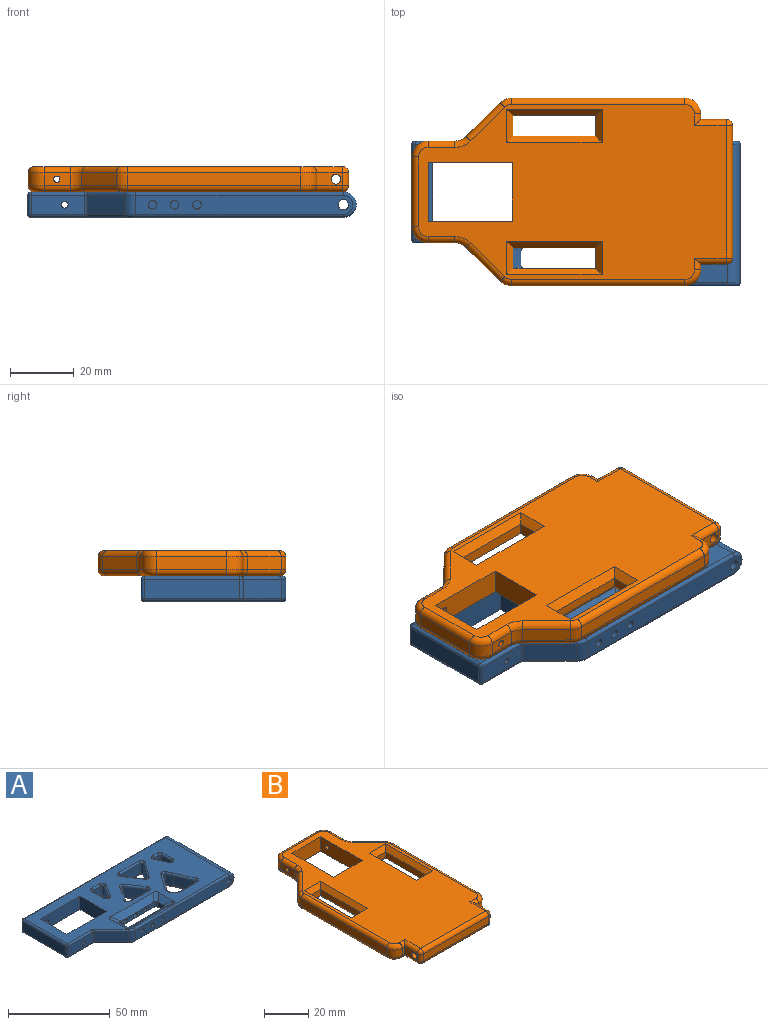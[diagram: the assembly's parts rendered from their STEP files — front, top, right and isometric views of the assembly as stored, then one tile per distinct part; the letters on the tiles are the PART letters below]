
ASSEMBLY  parts=2 mates=1
PART A: 177 faces, bbox 103.4x45.9x8.7 mm
  f0: cylinder r=1.05mm len=6.8mm, axis (0,1,0), area 44.9mm2, adj f19,f122
  f1: cylinder r=1.05mm len=6.8mm, axis (0,1,0), area 44.9mm2, adj f2,f79
  f2: plane 101.1x6mm, normal (0,1,0), area 590.7mm2, adj f1,f4,f5,f163,f164,f175
  f3: cylinder r=1mm len=65.22mm, axis (1,0,0), area 102.5mm2, adj f6,f8,f75,f165
  f4: cylinder r=1mm len=98.1mm, axis (1,0,0), area 154.1mm2, adj f2,f9,f163,f176
  f5: cylinder r=1mm len=98.1mm, axis (-1,0,0), area 154.1mm2, adj f2,f8,f163,f173
  f6: plane 68.22x6mm, normal (0,-1,0), area 379.7mm2, adj f3,f7,f76,f81,f83,f90,f164,f165
  f7: cylinder r=1mm len=65.22mm, axis (-1,0,0), area 102.5mm2, adj f6,f9,f77,f165
  f8: plane 98.1x43.5mm, normal (0,0,-1), area 2327mm2, adj f3,f5,f10,f11,f16,f17,f19,f25
  f9: plane 98.1x43.5mm, normal (0,0,1), area 2327mm2, adj f4,f7,f12,f13,f19,f20,f21,f22
  f10: cylinder r=1mm len=11.44mm, axis (0.59,0.81,0), area 21.1mm2, adj f8,f14,f93,f148
  f11: cylinder r=1mm len=11.98mm, axis (-1,0,0), area 18.8mm2, adj f8,f15,f97,f135
  f12: cylinder r=1mm len=11.98mm, axis (1,0,0), area 18.8mm2, adj f9,f15,f31,f136
  f13: cylinder r=1mm len=11.44mm, axis (-0.59,-0.81,0), area 21.1mm2, adj f9,f14,f95,f150
  f14: plane 10.85x7.9mm, normal (0.81,-0.59,0), area 80.5mm2, adj f10,f13,f92,f143
  f15: plane 11.98x6mm, normal (0,1,0), area 71.9mm2, adj f11,f12,f130,f138
  f16: cylinder r=3mm len=5.62mm, axis (0.63,-0.63,0.44), area 14mm2, adj f8,f17,f24,f68,f84,f88
  f17: plane 10.2x3.57mm, normal (0.57,0,-0.82), area 28.9mm2, adj f8,f16,f25,f88
  f18: cylinder r=1mm len=6mm, axis (0,0,-1), area 4.7mm2, adj f69,f70,f102,f122
  f19: plane 27.5x8mm, normal (0,1,0), area 216.5mm2, adj f0,f8,f9,f80,f168
  f20: plane 29.7x3.57mm, normal (0,0.57,0.82), area 113.9mm2, adj f9,f82,f101,f107
  f21: cylinder r=1mm len=7.99mm, axis (0,-1,0), area 12.5mm2, adj f9,f48,f49,f126
  f22: cylinder r=3mm len=5.62mm, axis (-0.63,-0.63,-0.44), area 14mm2, adj f9,f23,f27,f84,f87,f91
  f23: cylinder r=1mm len=3.12mm, axis (0,0,-1), area 4.9mm2, adj f22,f27,f84,f131
  f24: cylinder r=1mm len=3.12mm, axis (0,0,-1), area 4.9mm2, adj f16,f84,f88,f132
  f25: cylinder r=3mm len=5.62mm, axis (0.63,0.63,0.44), area 14mm2, adj f8,f17,f30,f82,f85,f88
  f26: torus R=2mm, axis (0,0,-1), area 4.6mm2, adj f9,f46,f47,f105
  f27: plane 4.52x3.14mm, normal (-1,0,0), area 13.6mm2, adj f22,f23,f86,f87,f99,f100,f101,f131
  f28: torus R=2mm, axis (0,0,-1), area 4.2mm2, adj f9,f64,f67,f106
  f29: cylinder r=1mm len=1mm, axis (0,-1,0), area 1.5mm2, adj f9,f32,f95,f124
  f30: cylinder r=1mm len=3.12mm, axis (0,0,-1), area 4.9mm2, adj f25,f82,f88,f107
  f31: torus R=2mm, axis (0,0,-1), area 1.7mm2, adj f9,f12,f33,f130
  f32: torus R=2mm, axis (0,0,-1), area 1.7mm2, adj f9,f29,f33,f129
  f33: cylinder r=1mm len=3.12mm, axis (0.71,-0.71,0), area 5.4mm2, adj f9,f31,f32,f121
  f34: torus R=2mm, axis (0,0,-1), area 4.7mm2, adj f8,f35,f36,f118
  f35: cylinder r=1mm len=13.73mm, axis (1,0,0), area 21.6mm2, adj f8,f34,f37,f125
  f36: cylinder r=1mm len=10.38mm, axis (-0.59,-0.81,0), area 19mm2, adj f8,f34,f38,f112
  f37: torus R=2mm, axis (0,0,-1), area 4.6mm2, adj f8,f35,f39,f119
  f38: torus R=2mm, axis (0,0,-1), area 4.1mm2, adj f8,f36,f39,f116
  f39: cylinder r=1mm len=10.35mm, axis (-0.56,0.83,0), area 18.5mm2, adj f8,f37,f38,f113
  f40: torus R=2mm, axis (0,0,-1), area 4.6mm2, adj f8,f41,f42,f105
  f41: cylinder r=1mm len=5.32mm, axis (1,0,0), area 8.4mm2, adj f8,f40,f43,f89
  f42: cylinder r=1mm len=8.54mm, axis (-0.55,-0.83,0), area 15.1mm2, adj f8,f40,f44,f117
  f43: torus R=2mm, axis (0,0,-1), area 3.4mm2, adj f8,f41,f45,f120
  f44: torus R=2mm, axis (0,0,-1), area 5.5mm2, adj f8,f42,f45,f110
  f45: cylinder r=1mm len=7.99mm, axis (0,1,0), area 12.5mm2, adj f8,f43,f44,f126
  f46: cylinder r=1mm len=8.54mm, axis (0.55,0.83,0), area 15.1mm2, adj f9,f26,f48,f117
  f47: cylinder r=1mm len=5.32mm, axis (-1,0,0), area 8.4mm2, adj f9,f26,f49,f89
  f48: torus R=2mm, axis (0,0,-1), area 5.5mm2, adj f9,f21,f46,f110
  f49: torus R=2mm, axis (0,0,-1), area 3.4mm2, adj f9,f21,f47,f120
  f50: torus R=2mm, axis (0,0,-1), area 4.7mm2, adj f9,f51,f52,f118
  f51: cylinder r=1mm len=10.38mm, axis (0.59,0.81,0), area 19mm2, adj f9,f50,f53,f112
  f52: cylinder r=1mm len=13.73mm, axis (-1,0,0), area 21.6mm2, adj f9,f50,f54,f125
  f53: torus R=2mm, axis (0,0,-1), area 4.1mm2, adj f9,f51,f55,f116
  f54: torus R=2mm, axis (0,0,-1), area 4.6mm2, adj f9,f52,f55,f119
  f55: cylinder r=1mm len=10.35mm, axis (0.56,-0.83,0), area 18.5mm2, adj f9,f53,f54,f113
  f56: cylinder r=1mm len=6mm, axis (0,0,1), area 13mm2, adj f60,f66,f114,f115
  f57: torus R=2mm, axis (0,0,-1), area 4.6mm2, adj f8,f58,f59,f109
  f58: cylinder r=1mm len=12.77mm, axis (-1,0,0), area 20.1mm2, adj f8,f57,f60,f114
  f59: cylinder r=1mm len=10.08mm, axis (0.55,0.83,0), area 18mm2, adj f8,f57,f61,f123
  f60: torus R=2mm, axis (0,0,-1), area 4.6mm2, adj f8,f56,f58,f62
  f61: torus R=2mm, axis (0,0,-1), area 4.2mm2, adj f8,f59,f62,f106
  f62: cylinder r=1mm len=10.08mm, axis (0.56,-0.83,0), area 18mm2, adj f8,f60,f61,f115
  f63: torus R=2mm, axis (0,0,-1), area 4.6mm2, adj f9,f64,f65,f109
  f64: cylinder r=1mm len=10.08mm, axis (-0.55,-0.83,0), area 18mm2, adj f9,f28,f63,f123
  f65: cylinder r=1mm len=12.77mm, axis (1,0,0), area 20.1mm2, adj f9,f63,f66,f114
  f66: torus R=2mm, axis (0,0,-1), area 4.6mm2, adj f9,f56,f65,f67
  f67: cylinder r=1mm len=10.08mm, axis (-0.56,0.83,0), area 18mm2, adj f9,f28,f66,f115
  f68: plane 29.7x3.57mm, normal (0,-0.57,-0.82), area 113.9mm2, adj f8,f16,f84,f131
  f69: torus R=2mm, axis (0,0,-1), area 1.7mm2, adj f8,f18,f71,f72
  f70: torus R=2mm, axis (0,0,-1), area 1.7mm2, adj f9,f18,f73,f74
  f71: cylinder r=1mm len=16.89mm, axis (1,0,0), area 26.5mm2, adj f8,f69,f122,f169
  f72: cylinder r=1mm len=12.45mm, axis (0.71,-0.71,0), area 26.1mm2, adj f8,f69,f75,f102
  f73: cylinder r=1mm len=12.45mm, axis (-0.71,0.71,0), area 26.1mm2, adj f9,f70,f77,f102
  f74: cylinder r=1mm len=16.89mm, axis (-1,0,0), area 26.5mm2, adj f9,f70,f122,f172
  f75: torus R=4mm, axis (0,0,-1), area 5.7mm2, adj f3,f8,f72,f76
  f76: cylinder r=5mm len=6mm, axis (0,0,1), area 23.6mm2, adj f6,f75,f77,f102
  f77: torus R=4mm, axis (0,0,-1), area 5.7mm2, adj f7,f9,f73,f76
  f78: plane 2.7x2.7mm, normal (0,-1,0), area 5.7mm2, adj f127
  f79: plane 27.5x8mm, normal (0,-1,0), area 216.5mm2, adj f1,f8,f9,f80,f168
  f80: plane 18.4x8mm, normal (-1,0,0), area 147.2mm2, adj f8,f9,f19,f79
  f81: cylinder r=1.35mm len=5.5mm, axis (0,1,0), area 46.7mm2, adj f6,f82
  f82: plane 24.02x3.14mm, normal (0,1,0), area 54.9mm2, adj f20,f25,f30,f81,f83,f85,f90,f99
  f83: cylinder r=1.35mm len=5.5mm, axis (0,1,0), area 46.7mm2, adj f6,f82
  f84: plane 24.02x3.14mm, normal (0,-1,0), area 54.9mm2, adj f16,f22,f23,f24,f68,f91,f103,f108
  f85: plane 29.7x3.57mm, normal (0,0.57,-0.82), area 113.9mm2, adj f8,f25,f82,f99
  f86: plane 10.2x3.57mm, normal (-0.57,0,-0.82), area 28.9mm2, adj f8,f27,f99,f131
  f87: plane 10.2x3.57mm, normal (-0.57,0,0.82), area 28.9mm2, adj f9,f22,f27,f101
  f88: plane 4.52x3.14mm, normal (1,0,0), area 13.6mm2, adj f16,f17,f24,f25,f30,f107,f128,f132
  f89: plane 6x5.32mm, normal (0,-1,0), area 31.9mm2, adj f41,f47,f105,f120
  f90: cylinder r=1.35mm len=5.5mm, axis (0,1,0), area 46.7mm2, adj f6,f82
  f91: plane 29.7x3.57mm, normal (0,-0.57,0.82), area 113.9mm2, adj f9,f22,f84,f132
  f92: cylinder r=1mm len=6mm, axis (0,0,-1), area 3.8mm2, adj f14,f93,f95,f124
  f93: torus R=2mm, axis (0,0,-1), area 1.3mm2, adj f8,f10,f92,f94
  f94: cylinder r=1mm len=1mm, axis (0,1,0), area 1.5mm2, adj f8,f93,f98,f124
  f95: torus R=2mm, axis (0,0,-1), area 1.3mm2, adj f9,f13,f29,f92
  f96: cylinder r=1mm len=3.12mm, axis (-0.71,0.71,0), area 5.4mm2, adj f8,f97,f98,f121
  f97: torus R=2mm, axis (0,0,-1), area 1.7mm2, adj f8,f11,f96,f130
  f98: torus R=2mm, axis (0,0,-1), area 1.7mm2, adj f8,f94,f96,f129
  f99: cylinder r=3mm len=5.62mm, axis (-0.63,0.63,0.44), area 14mm2, adj f8,f27,f82,f85,f86,f100
  f100: cylinder r=1mm len=3.12mm, axis (0,0,-1), area 4.9mm2, adj f27,f82,f99,f101
  f101: cylinder r=3mm len=5.62mm, axis (-0.63,0.63,-0.44), area 14mm2, adj f9,f20,f27,f82,f87,f100
  f102: plane 11.74x11.74mm, normal (-0.71,-0.71,0), area 99.6mm2, adj f18,f72,f73,f76
  f103: cylinder r=1.35mm len=4.5mm, axis (0,1,0), area 38.2mm2, adj f84,f104
  f104: plane 2.7x2.7mm, normal (0,-1,0), area 5.7mm2, adj f103
  f105: cylinder r=1mm len=6mm, axis (0,0,-1), area 13mm2, adj f26,f40,f89,f117
  f106: cylinder r=1mm len=6mm, axis (0,0,-1), area 11.8mm2, adj f28,f61,f115,f123
  f107: cylinder r=3mm len=5.62mm, axis (0.63,0.63,-0.44), area 14mm2, adj f9,f20,f30,f82,f88,f128
  f108: cylinder r=1.35mm len=4.5mm, axis (0,1,0), area 38.2mm2, adj f84,f111
  f109: cylinder r=1mm len=6mm, axis (0,0,-1), area 13mm2, adj f57,f63,f114,f123
  f110: cylinder r=1mm len=6mm, axis (0,0,1), area 15.3mm2, adj f44,f48,f117,f126
  f111: plane 2.7x2.7mm, normal (0,-1,0), area 5.7mm2, adj f108
  f112: plane 9.79x7.13mm, normal (-0.81,0.59,0), area 72.7mm2, adj f36,f51,f116,f118
  f113: plane 9.79x6.6mm, normal (0.83,0.56,0), area 70.9mm2, adj f39,f55,f116,f119
  f114: plane 12.77x6mm, normal (0,1,0), area 76.6mm2, adj f56,f58,f65,f109
  f115: plane 9.52x6.42mm, normal (-0.83,-0.56,0), area 68.9mm2, adj f56,f62,f67,f106
  f116: cylinder r=1mm len=6mm, axis (0,0,1), area 11.5mm2, adj f38,f53,f112,f113
  f117: plane 7.99x6mm, normal (-0.83,0.55,0), area 57.6mm2, adj f42,f46,f105,f110
  f118: cylinder r=1mm len=6mm, axis (0,0,-1), area 13.2mm2, adj f34,f50,f112,f125
  f119: cylinder r=1mm len=6mm, axis (0,0,1), area 13mm2, adj f37,f54,f113,f125
  f120: cylinder r=1mm len=6mm, axis (0,0,-1), area 9.4mm2, adj f43,f49,f89,f126
  f121: plane 6x2.41mm, normal (0.71,0.71,0), area 20.5mm2, adj f33,f96,f129,f130
  f122: plane 16.89x6mm, normal (0,-1,0), area 97.9mm2, adj f0,f18,f71,f74,f170
  f123: plane 9.52x6.35mm, normal (0.83,-0.55,0), area 68.7mm2, adj f59,f64,f106,f109
  f124: plane 6x0.97mm, normal (1,0,0), area 5.8mm2, adj f29,f92,f94,f129
  f125: plane 13.73x6mm, normal (0,-1,0), area 82.4mm2, adj f35,f52,f118,f119
  f126: plane 7.99x6mm, normal (1,0,0), area 47.9mm2, adj f21,f45,f110,f120
  f127: cylinder r=1.35mm len=4.5mm, axis (0,1,0), area 38.2mm2, adj f78,f84
  f128: plane 10.2x3.57mm, normal (0.57,0,0.82), area 28.9mm2, adj f9,f88,f107,f132
  f129: cylinder r=1mm len=6mm, axis (0,0,-1), area 4.7mm2, adj f32,f98,f121,f124
  f130: cylinder r=1mm len=6mm, axis (0,0,-1), area 4.7mm2, adj f15,f31,f97,f121
  f131: cylinder r=3mm len=5.62mm, axis (-0.63,-0.63,0.44), area 14mm2, adj f8,f23,f27,f68,f84,f86
  f132: cylinder r=3mm len=5.62mm, axis (0.63,-0.63,-0.44), area 14mm2, adj f9,f24,f84,f88,f91,f128
  f133: plane 10.64x6mm, normal (-0.91,-0.42,0), area 70.2mm2, adj f134,f137,f138,f139
  f134: cylinder r=1mm len=13.05mm, axis (0.42,-0.91,0), area 20.1mm2, adj f8,f133,f135,f147
  f135: torus R=2mm, axis (0,0,-1), area 4.3mm2, adj f8,f11,f134,f138
  f136: torus R=2mm, axis (0,0,-1), area 4.3mm2, adj f9,f12,f137,f138
  f137: cylinder r=1mm len=13.05mm, axis (-0.42,0.91,0), area 20.1mm2, adj f9,f133,f136,f149
  f138: cylinder r=1mm len=6mm, axis (0,0,1), area 12mm2, adj f15,f133,f135,f136
  f139: plane 6x3.59mm, normal (-0.91,-0.42,0), area 23.7mm2, adj f133,f143,f147,f149
  f140: plane 6x3.11mm, normal (0,-1,0), area 18.6mm2, adj f144,f146,f154,f160
  f141: plane 6.81x6mm, normal (-1,0,0), area 40.9mm2, adj f145,f146,f151,f161
  f142: plane 6.81x6mm, normal (0.91,0.42,0), area 44.9mm2, adj f144,f145,f155,f157
  f143: cylinder r=1mm len=6mm, axis (0,0,1), area 12.5mm2, adj f14,f139,f148,f150
  f144: cylinder r=1mm len=6mm, axis (0,0,-1), area 12mm2, adj f140,f142,f156,f158
  f145: cylinder r=1mm len=6mm, axis (0,0,-1), area 16.3mm2, adj f141,f142,f153,f159
  f146: cylinder r=1mm len=6mm, axis (0,0,-1), area 9.4mm2, adj f140,f141,f152,f162
  f147: cylinder r=1mm len=4.01mm, axis (0.42,-0.91,0), area 4.5mm2, adj f8,f134,f139,f148
  f148: torus R=2mm, axis (0,0,-1), area 4.5mm2, adj f8,f10,f143,f147
  f149: cylinder r=1mm len=4.01mm, axis (-0.42,0.91,0), area 4.5mm2, adj f9,f137,f139,f150
  f150: torus R=2mm, axis (0,0,-1), area 4.5mm2, adj f9,f13,f143,f149
  f151: cylinder r=1mm len=6.81mm, axis (0,-1,0), area 10.7mm2, adj f8,f141,f152,f153
  f152: torus R=2mm, axis (0,0,-1), area 3.4mm2, adj f8,f146,f151,f154
  f153: torus R=2mm, axis (0,0,-1), area 5.8mm2, adj f8,f145,f151,f155
  f154: cylinder r=1mm len=3.11mm, axis (1,0,0), area 4.9mm2, adj f8,f140,f152,f156
  f155: cylinder r=1mm len=7.22mm, axis (-0.42,0.91,0), area 11.8mm2, adj f8,f142,f153,f156
  f156: torus R=2mm, axis (0,0,-1), area 4.3mm2, adj f8,f144,f154,f155
  f157: cylinder r=1mm len=7.22mm, axis (0.42,-0.91,0), area 11.8mm2, adj f9,f142,f158,f159
  f158: torus R=2mm, axis (0,0,-1), area 4.3mm2, adj f9,f144,f157,f160
  f159: torus R=2mm, axis (0,0,-1), area 5.8mm2, adj f9,f145,f157,f161
  f160: cylinder r=1mm len=3.11mm, axis (-1,0,0), area 4.9mm2, adj f9,f140,f158,f162
  f161: cylinder r=1mm len=6.81mm, axis (0,1,0), area 10.7mm2, adj f9,f141,f159,f162
  f162: torus R=2mm, axis (0,0,-1), area 3.4mm2, adj f9,f146,f160,f161
  f163: torus R=3mm, axis (0,-1,0), area 17.9mm2, adj f2,f4,f5,f166
  f164: cylinder r=1.65mm len=45.5mm, axis (0,1,0), area 471.7mm2, adj f2,f6
  f165: torus R=3mm, axis (0,1,0), area 17.9mm2, adj f3,f6,f7,f166
  f166: cylinder r=4mm len=43.5mm, axis (0,1,0), area 546.6mm2, adj f8,f9,f163,f165
  f167: plane 30x6mm, normal (-1,0,0), area 180mm2, adj f170,f171,f174,f175
  f168: plane 18.4x8mm, normal (1,0,0), area 147.2mm2, adj f8,f9,f19,f79
  f169: sphere r=1mm, area 1.6mm2, adj f71,f170,f171
  f170: cylinder r=1mm len=6mm, axis (0,0,1), area 9.4mm2, adj f122,f167,f169,f172
  f171: cylinder r=1mm len=30mm, axis (0,1,0), area 47.1mm2, adj f8,f167,f169,f173
  f172: sphere r=1mm, area 1.6mm2, adj f74,f170,f174
  f173: sphere r=1mm, area 2.1mm2, adj f5,f171,f175
  f174: cylinder r=1mm len=30mm, axis (0,1,0), area 47.1mm2, adj f9,f167,f172,f176
  f175: cylinder r=1mm len=6mm, axis (0,0,1), area 9.4mm2, adj f2,f167,f173,f176
  f176: sphere r=1mm, area 2.1mm2, adj f4,f174,f175
PART B: 99 faces, bbox 59.8x101x8 mm
  f0: plane 18.4x8mm, normal (0,1,0), area 147.2mm2, adj f1,f14,f15,f16
  f1: plane 26.5x8mm, normal (1,0,0), area 208.9mm2, adj f0,f2,f14,f15,f28
  f2: plane 18.4x8mm, normal (0,-1,0), area 147.2mm2, adj f1,f14,f15,f16
  f3: plane 21.97x4mm, normal (0,1,0), area 87.9mm2, adj f29,f33,f38,f55
  f4: plane 8.37x4mm, normal (-1,0,0), area 30.4mm2, adj f28,f33,f34,f39,f47
  f5: plane 10.83x10.63mm, normal (-0.71,0.7,0), area 60.7mm2, adj f34,f35,f43,f50
  f6: plane 54.42x4mm, normal (-1,0,0), area 217.7mm2, adj f35,f36,f49,f58
  f7: plane 4x1.73mm, normal (0,-1,0), area 6.9mm2, adj f8,f36,f57,f66
  f8: plane 8x4mm, normal (-1,0,0), area 24.9mm2, adj f7,f26,f61,f70,f71
  f9: plane 26x3mm, normal (-1,0,0), area 78mm2, adj f10,f12,f88,f96
  f10: plane 6.5x3mm, normal (0,1,0), area 19.5mm2, adj f9,f11,f90,f98
  f11: plane 26x3mm, normal (1,0,0), area 78mm2, adj f10,f12,f89,f97
  f12: plane 7.3x3.5mm, normal (0,-1,0), area 22.9mm2, adj f9,f11,f87,f88,f89,f95
  f13: plane 41.5x4mm, normal (0,-1,0), area 166mm2, adj f69,f70,f76,f77
  f14: plane 96.62x54.96mm, normal (0,0,1), area 3482.5mm2, adj f0,f1,f2,f16,f46,f47,f50,f51
  f15: plane 96.62x54.96mm, normal (0,0,-1), area 3456.8mm2, adj f0,f1,f2,f16,f37,f38,f39,f40
  f16: plane 26.5x8mm, normal (-1,0,0), area 208.9mm2, adj f0,f2,f14,f15,f27
  f17: plane 8.37x4mm, normal (1,0,0), area 30.4mm2, adj f27,f29,f30,f42,f63
  f18: plane 10.83x10.63mm, normal (0.71,0.7,0), area 60.7mm2, adj f30,f31,f48,f72
  f19: plane 54.42x4mm, normal (1,0,0), area 217.7mm2, adj f31,f32,f56,f78
  f20: plane 4x1.73mm, normal (0,-1,0), area 6.9mm2, adj f21,f32,f64,f82
  f21: plane 8x4mm, normal (1,0,0), area 24.9mm2, adj f20,f26,f68,f76,f81
  f22: plane 26x3mm, normal (1,0,0), area 78mm2, adj f23,f25,f84,f91
  f23: plane 6.9x3.5mm, normal (0,1,0), area 22.9mm2, adj f22,f24,f84,f86,f92
  f24: plane 26.4x3.5mm, normal (-1,0,0), area 91.1mm2, adj f23,f25,f83,f85,f94
  f25: plane 6.5x3mm, normal (0,-1,0), area 19.5mm2, adj f22,f24,f83,f93
  f26: cylinder r=1.5mm len=45.5mm, axis (1,0,0), area 428.8mm2, adj f8,f21
  f27: cylinder r=1mm len=6.79mm, axis (1,0,0), area 42.6mm2, adj f16,f17
  f28: cylinder r=1mm len=6.79mm, axis (1,0,0), area 42.6mm2, adj f1,f4
  f29: cylinder r=5mm len=5mm, axis (0,0,-1), area 31.4mm2, adj f3,f17,f40,f59
  f30: cylinder r=5mm len=4mm, axis (0,0,1), area 15.5mm2, adj f17,f18,f44,f67
  f31: cylinder r=5mm len=4mm, axis (0,0,-1), area 15.5mm2, adj f18,f19,f52,f75
  f32: cylinder r=5mm len=5mm, axis (0,0,-1), area 31.4mm2, adj f19,f20,f60,f80
  f33: cylinder r=5mm len=5mm, axis (0,0,-1), area 31.4mm2, adj f3,f4,f37,f51
  f34: cylinder r=5mm len=4mm, axis (0,0,1), area 15.5mm2, adj f4,f5,f41,f46
  f35: cylinder r=5mm len=4mm, axis (0,0,-1), area 15.5mm2, adj f5,f6,f45,f54
  f36: cylinder r=5mm len=5mm, axis (0,0,-1), area 31.4mm2, adj f6,f7,f53,f62
  f37: torus R=3mm, axis (0,0,1), area 21.1mm2, adj f15,f33,f38,f39
  f38: cylinder r=2mm len=21.97mm, axis (-1,0,0), area 69mm2, adj f3,f15,f37,f40
  f39: cylinder r=2mm len=8.37mm, axis (0,-1,0), area 26.3mm2, adj f4,f15,f37,f41
  f40: torus R=3mm, axis (0,0,1), area 21.1mm2, adj f15,f29,f38,f42
  f41: torus R=7mm, axis (0,0,1), area 14mm2, adj f15,f34,f39,f43
  f42: cylinder r=2mm len=8.37mm, axis (0,-1,0), area 26.3mm2, adj f15,f17,f40,f44
  f43: cylinder r=2mm len=12.23mm, axis (-0.7,-0.71,0), area 47.7mm2, adj f5,f15,f41,f45
  f44: torus R=7mm, axis (0,0,1), area 14mm2, adj f15,f30,f42,f48
  f45: torus R=3mm, axis (0,0,1), area 10.4mm2, adj f15,f35,f43,f49
  f46: torus R=7mm, axis (0,0,1), area 14mm2, adj f14,f34,f47,f50
  f47: cylinder r=2mm len=8.37mm, axis (0,1,0), area 26.3mm2, adj f4,f14,f46,f51
  f48: cylinder r=2mm len=12.23mm, axis (0.7,-0.71,0), area 47.7mm2, adj f15,f18,f44,f52
  f49: cylinder r=2mm len=54.42mm, axis (0,-1,0), area 171mm2, adj f6,f15,f45,f53
  f50: cylinder r=2mm len=12.23mm, axis (0.7,0.71,0), area 47.7mm2, adj f5,f14,f46,f54
  f51: torus R=3mm, axis (0,0,1), area 21.1mm2, adj f14,f33,f47,f55
  f52: torus R=3mm, axis (0,0,1), area 10.4mm2, adj f15,f31,f48,f56
  f53: torus R=3mm, axis (0,0,1), area 21.1mm2, adj f15,f36,f49,f57
  f54: torus R=3mm, axis (0,0,1), area 10.4mm2, adj f14,f35,f50,f58
  f55: cylinder r=2mm len=21.97mm, axis (1,0,0), area 69mm2, adj f3,f14,f51,f59
  f56: cylinder r=2mm len=54.42mm, axis (0,-1,0), area 171mm2, adj f15,f19,f52,f60
  f57: cylinder r=2mm len=3.73mm, axis (1,0,0), area 7.7mm2, adj f7,f15,f53,f61
  f58: cylinder r=2mm len=54.42mm, axis (0,1,0), area 171mm2, adj f6,f14,f54,f62
  f59: torus R=3mm, axis (0,0,1), area 21.1mm2, adj f14,f29,f55,f63
  f60: torus R=3mm, axis (0,0,1), area 21.1mm2, adj f15,f32,f56,f64
  f61: cylinder r=2mm len=10mm, axis (0,-1,0), area 27.4mm2, adj f8,f15,f57,f65
  f62: torus R=3mm, axis (0,0,1), area 21.1mm2, adj f14,f36,f58,f66
  f63: cylinder r=2mm len=8.37mm, axis (0,1,0), area 26.3mm2, adj f14,f17,f59,f67
  f64: cylinder r=2mm len=3.73mm, axis (-1,0,0), area 7.7mm2, adj f15,f20,f60,f68
  f65: sphere r=2mm, area 6.3mm2, adj f61,f69,f70
  f66: cylinder r=2mm len=3.73mm, axis (-1,0,0), area 7.7mm2, adj f7,f14,f62,f71
  f67: torus R=7mm, axis (0,0,1), area 14mm2, adj f14,f30,f63,f72
  f68: cylinder r=2mm len=10mm, axis (0,-1,0), area 27.4mm2, adj f15,f21,f64,f73
  f69: cylinder r=2mm len=41.5mm, axis (1,0,0), area 130.4mm2, adj f13,f15,f65,f73
  f70: cylinder r=2mm len=4mm, axis (0,0,-1), area 12.6mm2, adj f8,f13,f65,f74
  f71: cylinder r=2mm len=10mm, axis (0,1,0), area 27.4mm2, adj f8,f14,f66,f74
  f72: cylinder r=2mm len=12.23mm, axis (-0.7,0.71,0), area 47.7mm2, adj f14,f18,f67,f75
  f73: sphere r=2mm, area 6.3mm2, adj f68,f69,f76
  f74: sphere r=2mm, area 6.3mm2, adj f70,f71,f77
  f75: torus R=3mm, axis (0,0,1), area 10.4mm2, adj f14,f31,f72,f78
  f76: cylinder r=2mm len=4mm, axis (0,0,-1), area 12.6mm2, adj f13,f21,f73,f79
  f77: cylinder r=2mm len=41.5mm, axis (-1,0,0), area 130.4mm2, adj f13,f14,f74,f79
  f78: cylinder r=2mm len=54.42mm, axis (0,1,0), area 171mm2, adj f14,f19,f75,f80
  f79: sphere r=2mm, area 6.3mm2, adj f76,f77,f81
  f80: torus R=3mm, axis (0,0,1), area 21.1mm2, adj f14,f32,f78,f82
  f81: cylinder r=2mm len=10mm, axis (0,1,0), area 27.4mm2, adj f14,f21,f79,f82
  f82: cylinder r=2mm len=3.73mm, axis (1,0,0), area 7.7mm2, adj f14,f20,f80,f81
  f83: plane 11x2.5mm, normal (0,-0.78,-0.62), area 27.2mm2, adj f15,f24,f25,f84,f85
  f84: plane 30.5x2.5mm, normal (0.78,0,-0.62), area 89.6mm2, adj f15,f22,f23,f83,f86
  f85: plane 30.5x2.5mm, normal (-0.62,0,-0.78), area 91.1mm2, adj f15,f24,f83,f86
  f86: plane 11x2.5mm, normal (0,0.62,-0.78), area 28.7mm2, adj f15,f23,f84,f85
  f87: plane 10.5x2.5mm, normal (0,-0.62,-0.78), area 28.5mm2, adj f12,f15,f88,f89
  f88: plane 30.5x2.5mm, normal (-0.78,0,-0.62), area 89.6mm2, adj f9,f12,f15,f87,f90
  f89: plane 30.5x2.5mm, normal (0.78,0,-0.62), area 89.6mm2, adj f11,f12,f15,f87,f90
  f90: plane 10.5x2.5mm, normal (0,0.78,-0.62), area 27.2mm2, adj f10,f15,f88,f89
  f91: plane 30x2.5mm, normal (0.78,0,0.62), area 89.6mm2, adj f14,f22,f92,f93
  f92: plane 10.5x2.5mm, normal (0,0.78,0.62), area 27.2mm2, adj f14,f23,f91,f94
  f93: plane 10.5x2.5mm, normal (0,-0.78,0.62), area 27.2mm2, adj f14,f25,f91,f94
  f94: plane 30x2.5mm, normal (-0.78,0,0.62), area 89.6mm2, adj f14,f24,f92,f93
  f95: plane 10.5x2.5mm, normal (0,-0.78,0.62), area 27.2mm2, adj f12,f14,f96,f97
  f96: plane 30x2.5mm, normal (-0.78,0,0.62), area 89.6mm2, adj f9,f14,f95,f98
  f97: plane 30x2.5mm, normal (0.78,0,0.62), area 89.6mm2, adj f11,f14,f95,f98
  f98: plane 10.5x2.5mm, normal (0,0.78,0.62), area 27.2mm2, adj f10,f14,f96,f97
PLACE A t=(-13.08,-5.94,5.18)mm
PLACE B rot(axis=(0,0,1),90deg) t=(18.13,1.06,9.18)mm
MATE fastened B.f15 <-> A.f9  axis (0,0,-1) through (-52.83,-8.14,9.18)mm
